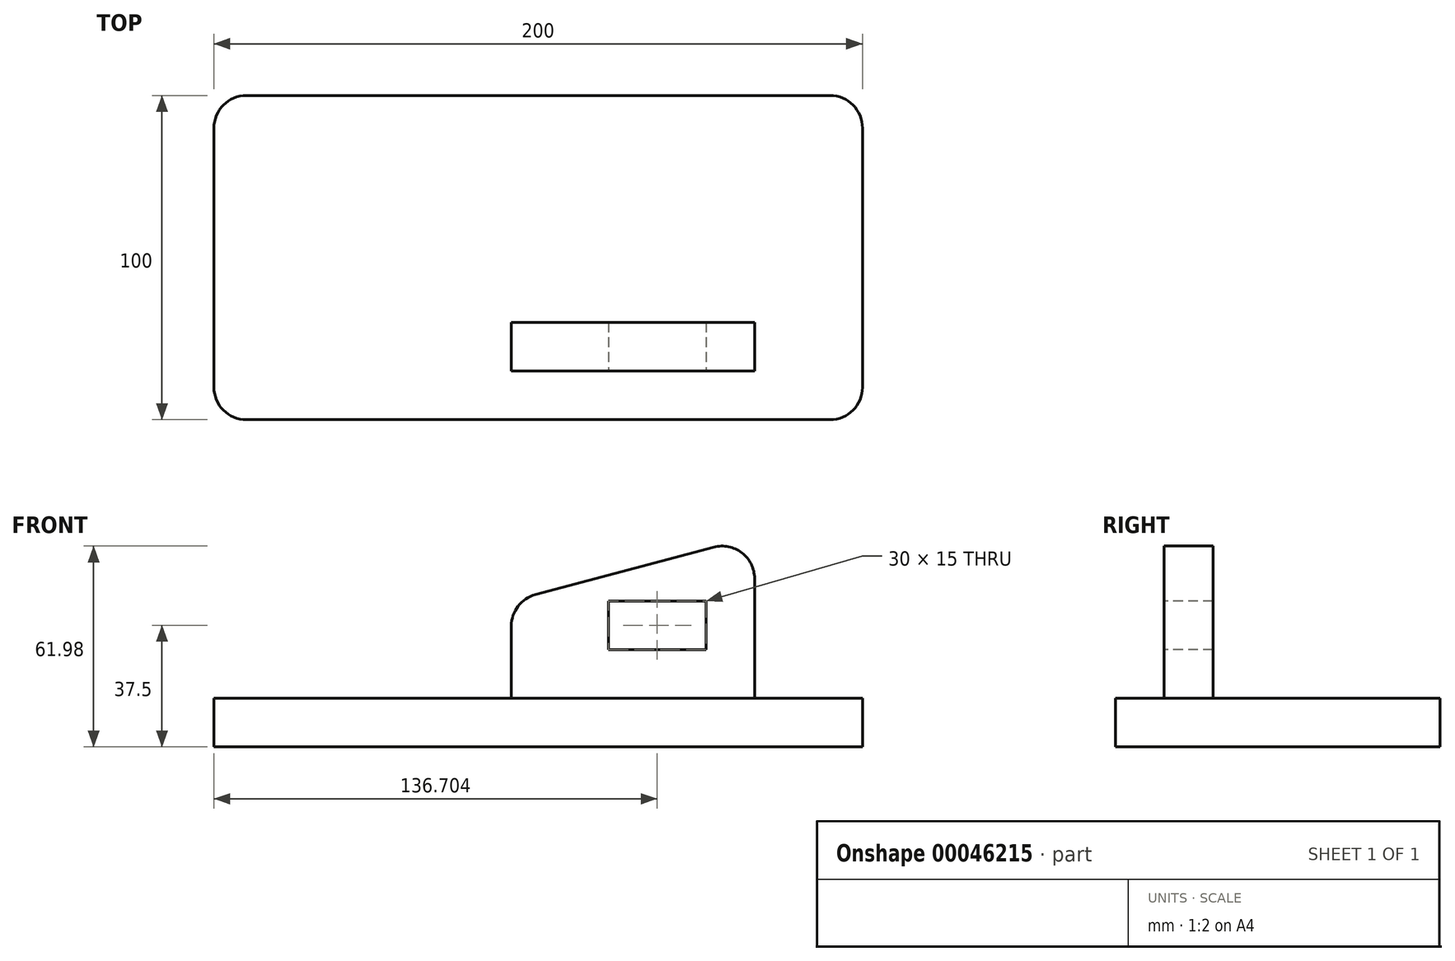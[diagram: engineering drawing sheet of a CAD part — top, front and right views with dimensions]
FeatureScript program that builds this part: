
annotation { "Feature Type Name" : "Feature", "Feature Type Description" : "" }
export const myFeature = defineFeature(function(context is Context, id is Id, definition is map)
    precondition{}
    {
        {
            var Q0;
            Q0=qCreatedBy(makeId("Top.planeOp"),FACE);
            var sketch = newSketch(context, id + "F0", { "sketchPlane" : qUnion([Q0])});
            skLineSegment(sketch, "E0.bottom", {"start": v(0, 0) * mm, "end": v(200, 0) * mm});
            skLineSegment(sketch, "E0.top", {"start": v(0, 100) * mm, "end": v(200, 100) * mm});
            skLineSegment(sketch, "E0.left", {"start": v(0, 0) * mm, "end": v(0, 100) * mm});
            skLineSegment(sketch, "E0.right", {"start": v(200, 0) * mm, "end": v(200, 100) * mm});
            skSolve(sketch);
        }
        {
            var Q0;
            Q0=makeQuery(id+"F0.imprint","IMPRINT",FACE,{"disambiguationData":[TD([[makeQuery(id+"F0.imprint","IMPRINT",EDGE,{"derivedFrom":sQuery(id+"F0.wireOp",EDGE,"E0.bottom")}),1.0]])]});
            extrude(context, id + "F1", {"entities" : qUnion([Q0]), "depth" : 15 * mm});
        }
        {
            var Q0;
            Q0=makeQuery(id+"F1.opExtrude","SWEPT_FACE",FACE,{"disambiguationData":[OSD([sQuery(id+"F0.wireOp",EDGE,"E0.bottom")])]});
            cPlane(context, id + "F2", {"entities" : qUnion([Q0]), "cplaneType" : CPlaneType.OFFSET, "offset" : 15 * mm, "oppositeDirection" : true, "width" : 150 * mm, "height" : 150 * mm});
        }
        {
            var Q0;
            Q0=qCreatedBy(id+"F2.planeOp",FACE);
            var sketch = newSketch(context, id + "F3", { "sketchPlane" : qUnion([Q0])});
            skLineSegment(sketch, "E1", {"start": v(166.7, 15) * mm, "end": v(166.7, 65) * mm});
            skLineSegment(sketch, "E2", {"start": v(166.7, 65) * mm, "end": v(91.7, 45) * mm});
            skLineSegment(sketch, "E3", {"start": v(91.7, 45) * mm, "end": v(91.7, 15) * mm});
            skLineSegment(sketch, "E4", {"start": v(91.7, 15) * mm, "end": v(166.7, 15) * mm});
            skLineSegment(sketch, "E5.bottom", {"start": v(121.7, 45) * mm, "end": v(151.7, 45) * mm});
            skLineSegment(sketch, "E5.top", {"start": v(121.7, 30) * mm, "end": v(151.7, 30) * mm});
            skLineSegment(sketch, "E5.left", {"start": v(121.7, 45) * mm, "end": v(121.7, 30) * mm});
            skLineSegment(sketch, "E5.right", {"start": v(151.7, 45) * mm, "end": v(151.7, 30) * mm});
            skSolve(sketch);
        }
        {
            var Q0;
            Q0=makeQuery(id+"F3.imprint","IMPRINT",FACE,{"disambiguationData":[TD([[makeQuery(id+"F3.imprint","IMPRINT",EDGE,{"derivedFrom":sQuery(id+"F3.wireOp",EDGE,"E1")}),1.0]])]});
            extrude(context, id + "F4", {"entities" : qUnion([Q0]), "operationType" : NewBodyOperationType.ADD, "oppositeDirection" : true, "depth" : 15 * mm});
        }
        {
            var Q0;
            Q0=makeQuery(id+"F1.opExtrude","SWEPT_EDGE",EDGE,{"disambiguationData":[OSD([sQuery(id+"F0.wireOp",EDGE,"E0.bottom"),sQuery(id+"F0.wireOp",EDGE,"E0.right")])]});
            var Q1;
            Q1=makeQuery(id+"F1.opExtrude","SWEPT_EDGE",EDGE,{"disambiguationData":[OSD([sQuery(id+"F0.wireOp",EDGE,"E0.top"),sQuery(id+"F0.wireOp",EDGE,"E0.right")])]});
            var Q2;
            Q2=makeQuery(id+"F1.opExtrude","SWEPT_EDGE",EDGE,{"disambiguationData":[OSD([sQuery(id+"F0.wireOp",EDGE,"E0.bottom"),sQuery(id+"F0.wireOp",EDGE,"E0.left")])]});
            var Q3;
            Q3=makeQuery(id+"F1.opExtrude","SWEPT_EDGE",EDGE,{"disambiguationData":[OSD([sQuery(id+"F0.wireOp",EDGE,"E0.top"),sQuery(id+"F0.wireOp",EDGE,"E0.left")])]});
            var Q4;
            Q4=makeQuery(id+"F4.opExtrude","SWEPT_EDGE",EDGE,{"disambiguationData":[OSD([sQuery(id+"F3.wireOp",EDGE,"E2"),sQuery(id+"F3.wireOp",EDGE,"E3")])]});
            var Q5;
            Q5=makeQuery(id+"F4.opExtrude","SWEPT_EDGE",EDGE,{"disambiguationData":[OSD([sQuery(id+"F3.wireOp",EDGE,"E1"),sQuery(id+"F3.wireOp",EDGE,"E2")])]});
            fillet(context, id + "F5", {"entities" : qUnion([Q0, Q1, Q2, Q3, Q4, Q5]), "radius" : 10 * mm, "tangentPropagation" : true, "allowEdgeOverflow" : false});
        }
    });
